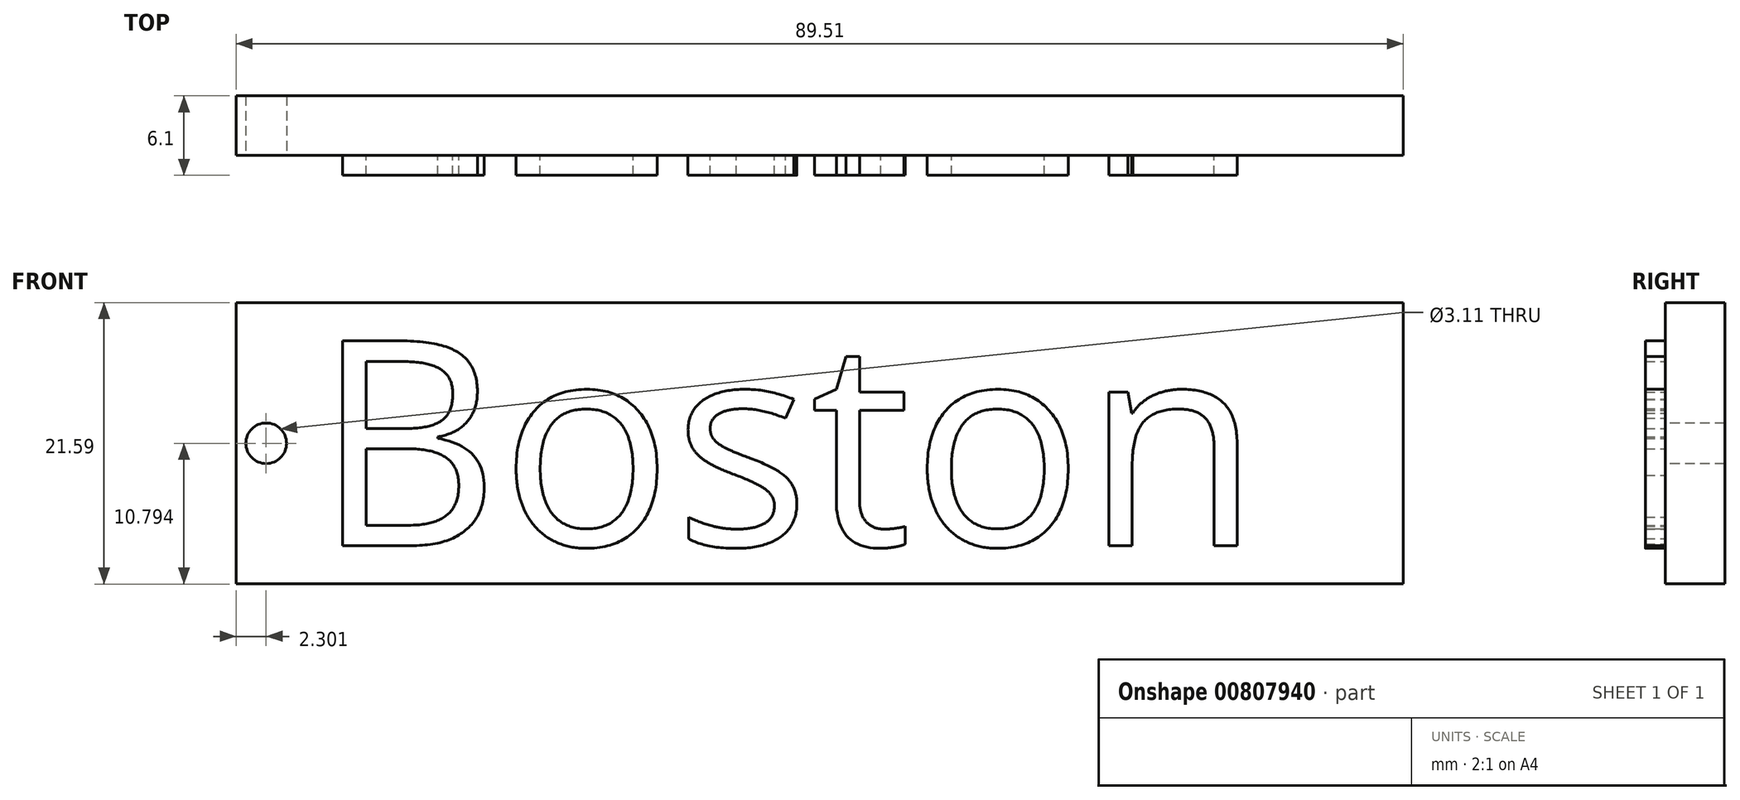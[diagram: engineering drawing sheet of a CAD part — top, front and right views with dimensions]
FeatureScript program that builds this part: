
annotation { "Feature Type Name" : "Feature", "Feature Type Description" : "" }
export const myFeature = defineFeature(function(context is Context, id is Id, definition is map)
    precondition{}
    {
        {
            var Q0;
            Q0=qCreatedBy(makeId("Front.planeOp"),FACE);
            var sketch = newSketch(context, id + "F0", { "sketchPlane" : qUnion([Q0])});
            skLineSegment(sketch, "E0.bottom", {"start": v(-51.66, 7.63) * mm, "end": v(37.85, 7.63) * mm});
            skLineSegment(sketch, "E0.top", {"start": v(-51.66, -13.96) * mm, "end": v(37.85, -13.96) * mm});
            skLineSegment(sketch, "E0.left", {"start": v(-51.66, 7.63) * mm, "end": v(-51.66, -13.96) * mm});
            skLineSegment(sketch, "E0.right", {"start": v(37.85, 7.63) * mm, "end": v(37.85, -13.96) * mm});
            skSolve(sketch);
        }
        {
            var Q0;
            Q0 = qSketchRegion(id + "F0", true);
            extrude(context, id + "F1", {"entities" : qUnion([Q0]), "depth" : 4.57 * mm, "offsetDistance" : 25.4 * mm});
        }
        {
            var Q0;
            Q0=makeQuery(id+"F1.opExtrude","CAP_FACE",FACE,{"disambiguationData":[OSD([sQuery(id+"F0.wireOp",EDGE,"E0.bottom"),sQuery(id+"F0.wireOp",EDGE,"E0.top"),sQuery(id+"F0.wireOp",EDGE,"E0.left"),sQuery(id+"F0.wireOp",EDGE,"E0.right")])],"isStart":false});
            var sketch = newSketch(context, id + "F2", { "sketchPlane" : qUnion([Q0])});
            skCircle(sketch, "E1", {"center": v(-49.36, -3.17) * mm, "radius": 1.56 * mm});
            skPoint(sketch, "E1.centerSnap0", {"position": v(-51.66, -3.17) * mm});
            skSolve(sketch);
        }
        {
            var Q0;
            Q0 = qSketchRegion(id + "F2", true);
            extrude(context, id + "F3", {"entities" : qUnion([Q0]), "operationType" : NewBodyOperationType.REMOVE, "oppositeDirection" : true, "depth" : 70.1 * mm, "offsetDistance" : 25.4 * mm});
        }
        {
            var Q0;
            Q0=makeQuery(id+"F1.opExtrude","CAP_FACE",FACE,{"disambiguationData":[OSD([sQuery(id+"F0.wireOp",EDGE,"E0.bottom"),sQuery(id+"F0.wireOp",EDGE,"E0.top"),sQuery(id+"F0.wireOp",EDGE,"E0.left"),sQuery(id+"F0.wireOp",EDGE,"E0.right")])],"isStart":false});
            var sketch = newSketch(context, id + "F4", { "sketchPlane" : qUnion([Q0])});
            skText(sketch, "E2", { "text": "Boston", "fontName": "OpenSans-Regular.ttf"});
            const initialGuessF4  = {"E2": [-0.04567, -0.01101, 1, 0, 0.01583]};
            skSetInitialGuess(sketch, initialGuessF4);
            skSolve(sketch);
        }
        {
            var Q0;
            Q0 = qSketchRegion(id + "F4", true);
            extrude(context, id + "F5", {"entities" : qUnion([Q0]), "operationType" : NewBodyOperationType.ADD, "depth" : 1.52 * mm, "offsetDistance" : 25.4 * mm});
        }
    });
